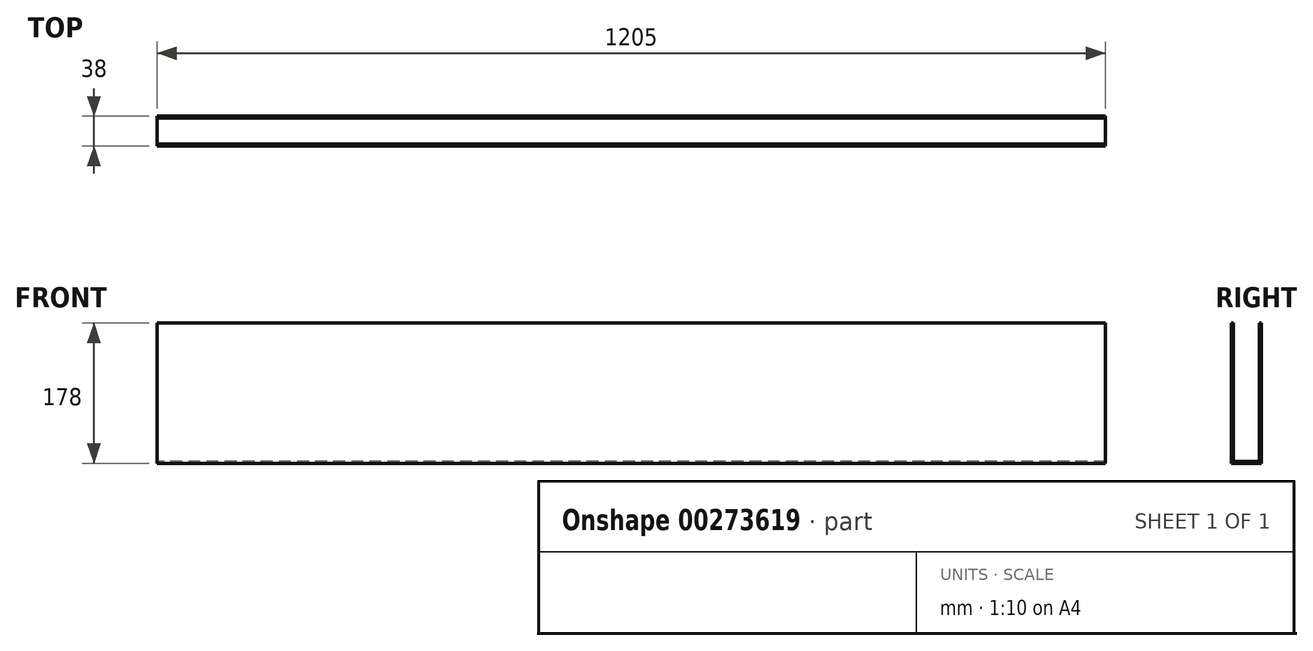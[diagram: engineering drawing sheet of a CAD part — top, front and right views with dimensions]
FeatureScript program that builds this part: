
annotation { "Feature Type Name" : "Feature", "Feature Type Description" : "" }
export const myFeature = defineFeature(function(context is Context, id is Id, definition is map)
    precondition{}
    {
        {
            var Q0;
            Q0=qCreatedBy(makeId("Right.planeOp"),FACE);
            var sketch = newSketch(context, id + "F0", { "sketchPlane" : qUnion([Q0])});
            skLineSegment(sketch, "E0", {"start": v(0, 0) * mm, "end": v(0, 175.5) * mm});
            skLineSegment(sketch, "E1", {"start": v(0, 0) * mm, "end": v(33, 0) * mm});
            skLineSegment(sketch, "E2", {"start": v(33, 0) * mm, "end": v(33, 175.5) * mm});
            skLineSegment(sketch, "E3.0", {"start": v(35.5, -2.5) * mm, "end": v(35.5, 175.5) * mm});
            skLineSegment(sketch, "E3.1", {"start": v(-2.5, -2.5) * mm, "end": v(35.5, -2.5) * mm});
            skLineSegment(sketch, "E3.2", {"start": v(-2.5, -2.5) * mm, "end": v(-2.5, 175.5) * mm});
            skLineSegment(sketch, "E4", {"start": v(-2.5, 175.5) * mm, "end": v(0, 175.5) * mm});
            skLineSegment(sketch, "E5", {"start": v(35.5, 175.5) * mm, "end": v(33, 175.5) * mm});
            skSolve(sketch);
        }
        {
            var Q0;
            Q0 = qSketchRegion(id + "F0", true);
            extrude(context, id + "F1", {"entities" : qUnion([Q0]), "depth" : 1205 * mm});
        }
    });
